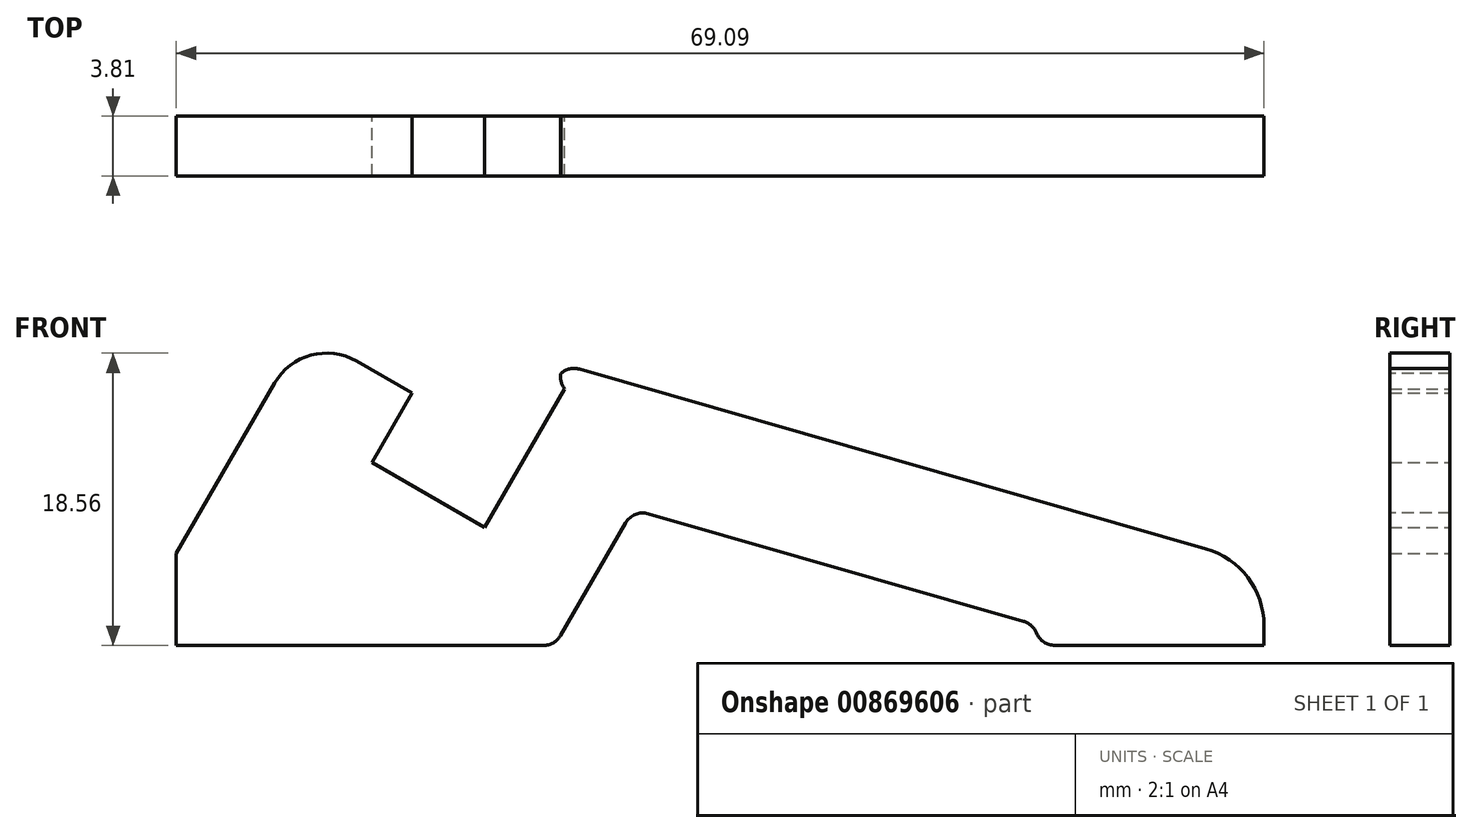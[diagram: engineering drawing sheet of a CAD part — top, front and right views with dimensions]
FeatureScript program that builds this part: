
annotation { "Feature Type Name" : "Feature", "Feature Type Description" : "" }
export const myFeature = defineFeature(function(context is Context, id is Id, definition is map)
    precondition{}
    {
        {
            var Q0;
            Q0=qCreatedBy(makeId("Front.planeOp"),FACE);
            var sketch = newSketch(context, id + "F0", { "sketchPlane" : qUnion([Q0])});
            skLineSegment(sketch, "E0", {"start": v(0, 0) * mm, "end": v(0, 5.84) * mm});
            skLineSegment(sketch, "E1", {"start": v(0, 5.84) * mm, "end": v(8.15, 19.96) * mm});
            skLineSegment(sketch, "E2", {"start": v(8.15, 19.96) * mm, "end": v(14.97, 16.02) * mm});
            skLineSegment(sketch, "E3", {"start": v(14.97, 16.02) * mm, "end": v(12.43, 11.62) * mm});
            skLineSegment(sketch, "E4", {"start": v(12.43, 11.62) * mm, "end": v(19.58, 7.5) * mm});
            skLineSegment(sketch, "E5", {"start": v(19.58, 7.5) * mm, "end": v(24.66, 16.3) * mm});
            skLineSegment(sketch, "E6", {"start": v(24.66, 16.3) * mm, "end": v(24, 16.67) * mm});
            skLineSegment(sketch, "E7", {"start": v(24, 16.67) * mm, "end": v(24.66, 17.82) * mm});
            skLineSegment(sketch, "E8", {"start": v(69.09, 0) * mm, "end": v(0, 0) * mm});
            skLineSegment(sketch, "E9", {"start": v(69.09, 0) * mm, "end": v(69.09, 5.08) * mm});
            skLineSegment(sketch, "E10", {"start": v(69.09, 5.08) * mm, "end": v(24.66, 17.82) * mm});
            skLineSegment(sketch, "E11", {"start": v(54.73, 0) * mm, "end": v(54.73, 1.27) * mm});
            skLineSegment(sketch, "E12", {"start": v(54.73, 1.27) * mm, "end": v(29.04, 8.63) * mm});
            skLineSegment(sketch, "E13", {"start": v(29.04, 8.63) * mm, "end": v(24.05, 0) * mm});
            skSolve(sketch);
        }
        {
            var Q0;
            Q0=makeQuery(id+"F0.imprint","IMPRINT",FACE,{"disambiguationData":[TD([[makeQuery(id+"F0.imprint","IMPRINT",EDGE,{"derivedFrom":sQuery(id+"F0.wireOp",EDGE,"E0")}),-1.0]])]});
            extrude(context, id + "F1", {"entities" : qUnion([Q0]), "depth" : 3.8 * mm, "offsetDistance" : 25.4 * mm});
        }
        {
            var Q0;
            Q0=makeQuery(id+"F1.opExtrude","SWEPT_EDGE",EDGE,{"disambiguationData":[OSD([sQuery(id+"F0.wireOp",EDGE,"E7"),sQuery(id+"F0.wireOp",EDGE,"E10")])]});
            var Q1;
            Q1=makeQuery(id+"F1.opExtrude","SWEPT_EDGE",EDGE,{"disambiguationData":[OSD([sQuery(id+"F0.wireOp",EDGE,"E6"),sQuery(id+"F0.wireOp",EDGE,"E7")])]});
            fillet(context, id + "F2", {"entities" : qUnion([Q0, Q1]), "radius" : 1.27 * mm, "tangentPropagation" : true, "allowEdgeOverflow" : false});
        }
        {
            var Q0;
            Q0=makeQuery(id+"F1.opExtrude","SWEPT_EDGE",EDGE,{"disambiguationData":[OSD([sQuery(id+"F0.wireOp",EDGE,"E1"),sQuery(id+"F0.wireOp",EDGE,"E2")])]});
            fillet(context, id + "F3", {"entities" : qUnion([Q0]), "radius" : 3.8 * mm, "tangentPropagation" : true, "allowEdgeOverflow" : false});
        }
        {
            var Q0;
            Q0=makeQuery(id+"F1.opExtrude","SWEPT_EDGE",EDGE,{"disambiguationData":[OSD([sQuery(id+"F0.wireOp",EDGE,"E9"),sQuery(id+"F0.wireOp",EDGE,"E10")])]});
            fillet(context, id + "F4", {"entities" : qUnion([Q0]), "radius" : 5.08 * mm, "tangentPropagation" : true, "allowEdgeOverflow" : false});
        }
        {
            var Q0;
            Q0=makeQuery(id+"F1.opExtrude","SWEPT_EDGE",EDGE,{"disambiguationData":[OSD([sQuery(id+"F0.wireOp",EDGE,"E12"),sQuery(id+"F0.wireOp",EDGE,"E13")])]});
            var Q1;
            Q1=makeQuery(id+"F1.opExtrude","SWEPT_EDGE",EDGE,{"disambiguationData":[OSD([sQuery(id+"F0.wireOp",EDGE,"E8"),sQuery(id+"F0.wireOp",EDGE,"E13")])]});
            var Q2;
            Q2=makeQuery(id+"F1.opExtrude","SWEPT_EDGE",EDGE,{"disambiguationData":[OSD([sQuery(id+"F0.wireOp",EDGE,"E11"),sQuery(id+"F0.wireOp",EDGE,"E12")])]});
            fillet(context, id + "F5", {"entities" : qUnion([Q0, Q1, Q2]), "radius" : 1.27 * mm, "tangentPropagation" : true, "allowEdgeOverflow" : false});
        }
        {
            var Q0;
            Q0=makeQuery(id+"F1.opExtrude","SWEPT_EDGE",EDGE,{"disambiguationData":[OSD([sQuery(id+"F0.wireOp",EDGE,"E8"),sQuery(id+"F0.wireOp",EDGE,"E11")])]});
            fillet(context, id + "F6", {"entities" : qUnion([Q0]), "radius" : 1.27 * mm, "tangentPropagation" : true, "allowEdgeOverflow" : false});
        }
    });
